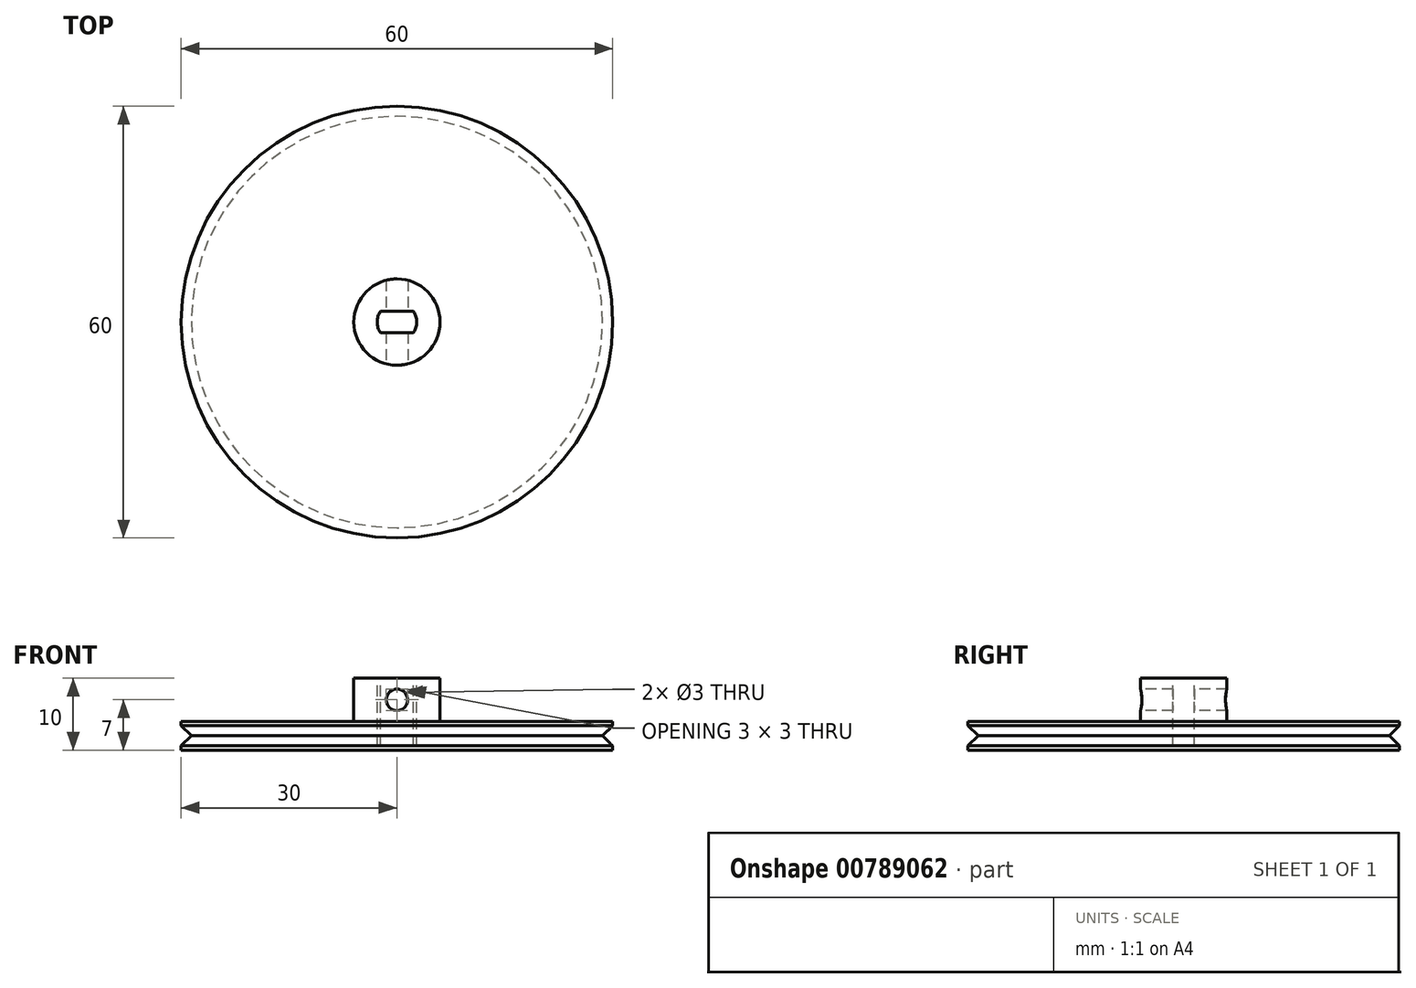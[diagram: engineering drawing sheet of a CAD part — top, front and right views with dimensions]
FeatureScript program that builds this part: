
annotation { "Feature Type Name" : "Feature", "Feature Type Description" : "" }
export const myFeature = defineFeature(function(context is Context, id is Id, definition is map)
    precondition{}
    {
        {
            var Q0;
            Q0=qCreatedBy(makeId("Top.planeOp"),FACE);
            var sketch = newSketch(context, id + "F0", { "sketchPlane" : qUnion([Q0])});
            skCircle(sketch, "E0", {"center": v(0, 0) * mm, "radius": 30 * mm});
            skCircle(sketch, "E1", {"center": v(0, 0) * mm, "radius": 6 * mm});
            skSolve(sketch);
        }
        {
            var Q0;
            Q0=makeQuery(id+"F0.imprint","IMPRINT",FACE,{"disambiguationData":[TD([[makeQuery(id+"F0.imprint","IMPRINT",EDGE,{"derivedFrom":sQuery(id+"F0.wireOp",EDGE,"E0")}),1.0]])]});
            var Q1;
            Q1=makeQuery(id+"F0.imprint","IMPRINT",FACE,{"disambiguationData":[TD([[makeQuery(id+"F0.imprint","IMPRINT",EDGE,{"derivedFrom":sQuery(id+"F0.wireOp",EDGE,"E1")}),1.0]])]});
            extrude(context, id + "F1", {"entities" : qUnion([Q0, Q1]), "oppositeDirection" : true, "depth" : 4 * mm, "offsetDistance" : 25 * mm});
        }
        {
            var Q0;
            Q0=makeQuery(id+"F0.imprint","IMPRINT",FACE,{"disambiguationData":[TD([[makeQuery(id+"F0.imprint","IMPRINT",EDGE,{"derivedFrom":sQuery(id+"F0.wireOp",EDGE,"E1")}),1.0]])]});
            extrude(context, id + "F2", {"entities" : qUnion([Q0]), "operationType" : NewBodyOperationType.ADD, "depth" : 6 * mm, "offsetDistance" : 25 * mm});
        }
        {
            var Q0;
            Q0=qCreatedBy(makeId("Front.planeOp"),FACE);
            var sketch = newSketch(context, id + "F3", { "sketchPlane" : qUnion([Q0])});
            skCircle(sketch, "E2", {"center": v(0, 3) * mm, "radius": 1.5 * mm});
            skSolve(sketch);
        }
        {
            var Q0;
            Q0 = qSketchRegion(id + "F3", true);
            extrude(context, id + "F4", {"entities" : qUnion([Q0]), "operationType" : NewBodyOperationType.REMOVE, "endBound" : BoundingType.SYMMETRIC, "oppositeDirection" : true, "depth" : 25 * mm, "offsetDistance" : 25 * mm});
        }
        {
            var Q0;
            Q0=makeQuery(id+"F2.opExtrude","CAP_FACE",FACE,{"disambiguationData":[OSD([sQuery(id+"F0.wireOp",EDGE,"E1")])],"isStart":false});
            var sketch = newSketch(context, id + "F5", { "sketchPlane" : qUnion([Q0])});
            skLineSegment(sketch, "E3.bottom", {"start": v(2.3, 1.5) * mm, "end": v(-2.3, 1.5) * mm});
            skLineSegment(sketch, "E3.top", {"start": v(2.3, -1.5) * mm, "end": v(-2.3, -1.5) * mm});
            skLineSegment(sketch, "E3.left", {"start": v(2.3, 1.5) * mm, "end": v(2.3, -1.5) * mm});
            skLineSegment(sketch, "E3.right", {"start": v(-2.3, 1.5) * mm, "end": v(-2.3, -1.5) * mm});
            skPoint(sketch, "E3.middle", {"position": v(0, 0) * mm});
            skArc(sketch, "E4", {"start": v(2.3, -1.5) * mm, "mid": v(2.75, 0) * mm, "end": v(2.3, 1.5) * mm});
            skArc(sketch, "E5", {"start": v(-2.3, 1.5) * mm, "mid": v(-2.75, 0) * mm, "end": v(-2.3, -1.5) * mm});
            skSolve(sketch);
        }
        {
            var Q0;
            Q0 = qSketchRegion(id + "F5", true);
            extrude(context, id + "F6", {"entities" : qUnion([Q0]), "operationType" : NewBodyOperationType.REMOVE, "oppositeDirection" : true, "depth" : 9.4 * mm, "offsetDistance" : 25 * mm});
        }
        {
            var Q0;
            Q0=qCreatedBy(makeId("Front.planeOp"),FACE);
            var sketch = newSketch(context, id + "F7", { "sketchPlane" : qUnion([Q0])});
            skLineSegment(sketch, "E6", {"start": v(0, -14.23) * mm, "end": v(0, 11.98) * mm, "construction": true});
            skLineSegment(sketch, "E7", {"start": v(30, 0) * mm, "end": v(30, -4) * mm, "construction": true});
            skLineSegment(sketch, "E8", {"start": v(30, 0) * mm, "end": v(30, -4) * mm});
            skLineSegment(sketch, "E9", {"start": v(30, -0.59) * mm, "end": v(28.59, -2) * mm});
            skLineSegment(sketch, "E10", {"start": v(28.59, -2) * mm, "end": v(30, -3.41) * mm});
            skLineSegment(sketch, "E11", {"start": v(30, -2) * mm, "end": v(26.36, -2) * mm, "construction": true});
            skSolve(sketch);
        }
        {
            var Q0;
            Q0 = qSketchRegion(id + "F7", true);
            var Q1;
            Q1=sQuery(id+"F7.wireOp",EDGE,"E6");
            revolve(context, id + "F8", {"operationType" : NewBodyOperationType.REMOVE, "surfaceOperationType" : NewSurfaceOperationType.NEW, "entities" : qUnion([Q0]), "axis" : qUnion([Q1]), "revolveType" : RevolveType.FULL, "oppositeDirection" : true});
        }
    });
